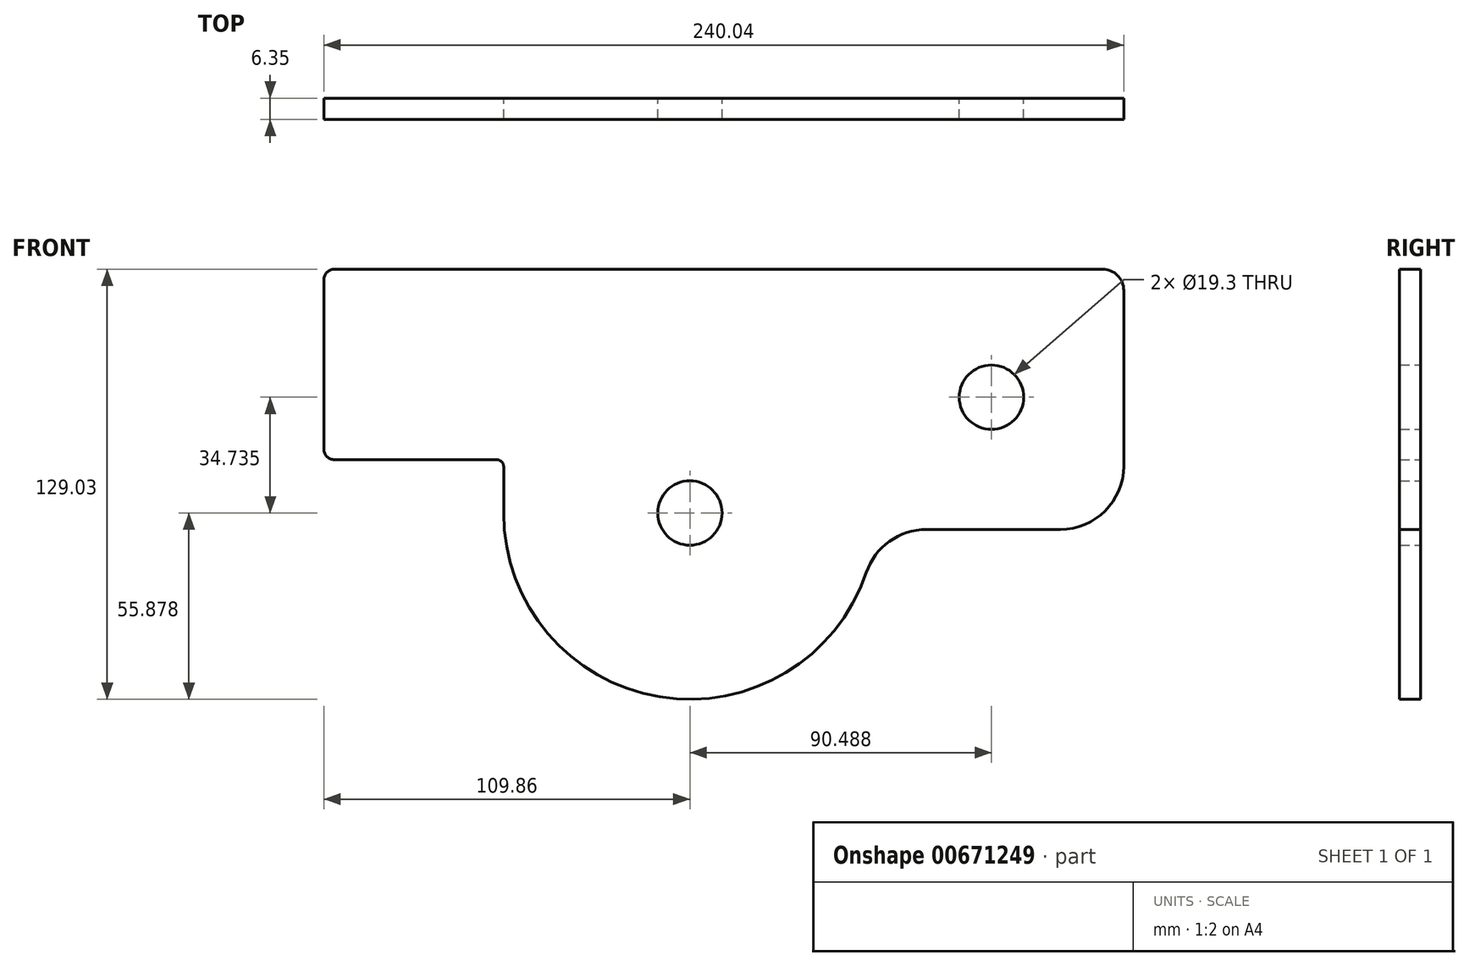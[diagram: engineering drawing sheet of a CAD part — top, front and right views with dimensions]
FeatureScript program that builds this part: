
annotation { "Feature Type Name" : "Feature", "Feature Type Description" : "" }
export const myFeature = defineFeature(function(context is Context, id is Id, definition is map)
    precondition{}
    {
        {
            var Q0;
            Q0=qCreatedBy(makeId("Front.planeOp"),FACE);
            var sketch = newSketch(context, id + "F0", { "sketchPlane" : qUnion([Q0])});
            skLineSegment(sketch, "E0", {"start": v(0, -59.18) * mm, "end": v(0, -73.15) * mm});
            skLineSegment(sketch, "E1", {"start": v(126.87, -78.1) * mm, "end": v(167, -78.1) * mm});
            skLineSegment(sketch, "E2", {"start": v(186.06, -59.04) * mm, "end": v(186.06, -6.35) * mm});
            skLineSegment(sketch, "E3", {"start": v(179.7, 0) * mm, "end": v(0, 0) * mm});
            skArc(sketch, "E4", {"start": v(0, -73.15) * mm, "mid": v(46.81, -128.3) * mm, "end": v(108.82, -91.04) * mm});
            skCircle(sketch, "E5", {"center": v(55.88, -73.15) * mm, "radius": 9.65 * mm});
            skPoint(sketch, "E6.visualSharp", {"position": v(39.05, -78.1) * mm});
            skPoint(sketch, "E7.visualSharp", {"position": v(186.06, -78.1) * mm});
            skArc(sketch, "E7.filletArc", {"start": v(167, -78.1) * mm, "mid": v(180.48, -72.51) * mm, "end": v(186.06, -59.04) * mm});
            skPoint(sketch, "E8.visualSharp", {"position": v(0, 0) * mm});
            skPoint(sketch, "E9.visualSharp", {"position": v(186.06, 0) * mm});
            skArc(sketch, "E9.filletArc", {"start": v(186.06, -6.35) * mm, "mid": v(184.2, -1.86) * mm, "end": v(179.7, 0) * mm});
            skCircle(sketch, "E10", {"center": v(146.37, -38.42) * mm, "radius": 9.65 * mm});
            skPoint(sketch, "E11.orphan", {"position": v(111.76, -73.15) * mm});
            skPoint(sketch, "E12.visualSharp", {"position": v(111.54, -78.1) * mm});
            skArc(sketch, "E12.filletArc", {"start": v(126.87, -78.1) * mm, "mid": v(115.76, -81.67) * mm, "end": v(108.82, -91.04) * mm});
            skLineSegment(sketch, "E13", {"start": v(-53.98, -3.18) * mm, "end": v(-53.98, -53.98) * mm});
            skLineSegment(sketch, "E14", {"start": v(-50.8, -57.15) * mm, "end": v(-2.03, -57.15) * mm});
            skLineSegment(sketch, "E15", {"start": v(0, 0) * mm, "end": v(-50.8, 0) * mm});
            skPoint(sketch, "E16.visualSharp", {"position": v(-53.98, 0) * mm});
            skArc(sketch, "E16.filletArc", {"start": v(-50.8, 0) * mm, "mid": v(-53.05, -0.93) * mm, "end": v(-53.98, -3.18) * mm});
            skPoint(sketch, "E17.visualSharp", {"position": v(-53.97, -57.15) * mm});
            skArc(sketch, "E17.filletArc", {"start": v(-53.97, -53.98) * mm, "mid": v(-53.05, -56.22) * mm, "end": v(-50.8, -57.15) * mm});
            skPoint(sketch, "E18.visualSharp", {"position": v(0, -57.15) * mm});
            skArc(sketch, "E18.filletArc", {"start": v(0, -59.18) * mm, "mid": v(-0.6, -57.75) * mm, "end": v(-2.03, -57.15) * mm});
            skSolve(sketch);
        }
        {
            var Q0;
            Q0 = qSketchRegion(id + "F0", true);
            extrude(context, id + "F1", {"entities" : qUnion([Q0]), "depth" : 6.35 * mm, "offsetDistance" : 25.4 * mm});
        }
    });
